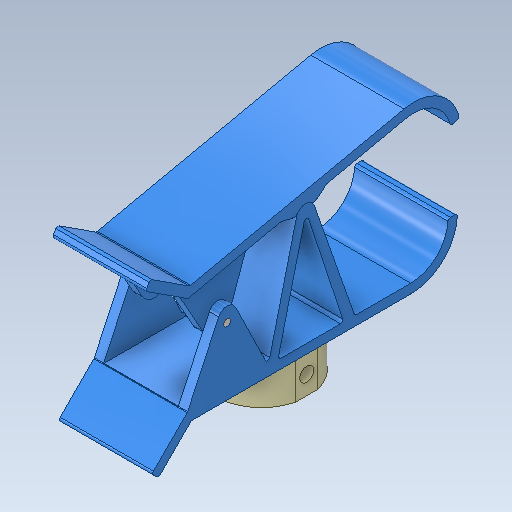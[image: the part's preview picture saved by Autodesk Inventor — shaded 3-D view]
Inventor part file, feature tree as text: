
AUTODESK INVENTOR PART (.ipt)
format: ipt  version: 2020 (Build 240168000, 168)  size: 286,720 bytes
history: native  units: mm
features: sketch x8, extrude x7, other x3
ambient origin geometry x8: Origin, YZ Plane, XZ Plane, XY Plane, X Axis, Y Axis, Z Axis, Center Point
bodies: Body1 (feature_tree), Body2 (feature_tree), Body3 (feature_tree), Body4 (feature_tree)
feature tree (18):
  sketch  "Эскиз1"
  extrude  "Выдавливание2"  Depth=8.0mm TaperAngle=0.0deg
  extrude  "Выдавливание3"  Depth=0.5mm
  extrude  "Выдавливание4"  Depth=20.0mm TaperAngle=0.0deg
  extrude  "Выдавливание5"  Depth=20.0mm TaperAngle=0.0deg
  extrude  "Выдавливание6"  Depth=20.0mm TaperAngle=0.0deg
  extrude  "Выдавливание7"  Depth=20.0mm TaperAngle=0.0deg
  extrude  "Выдавливание8"  Depth=20.0mm TaperAngle=0.0deg
  sketch  "Эскиз2"
  sketch  "Эскиз3"
  sketch  "Эскиз4"
  sketch  "Эскиз5"
  sketch  "Эскиз6"
  other  "Твердое тело3"
  sketch  "Эскиз7"
  other  "Твердое тело4"
  other  "Твердое тело5"
  sketch  "Эскиз8"
